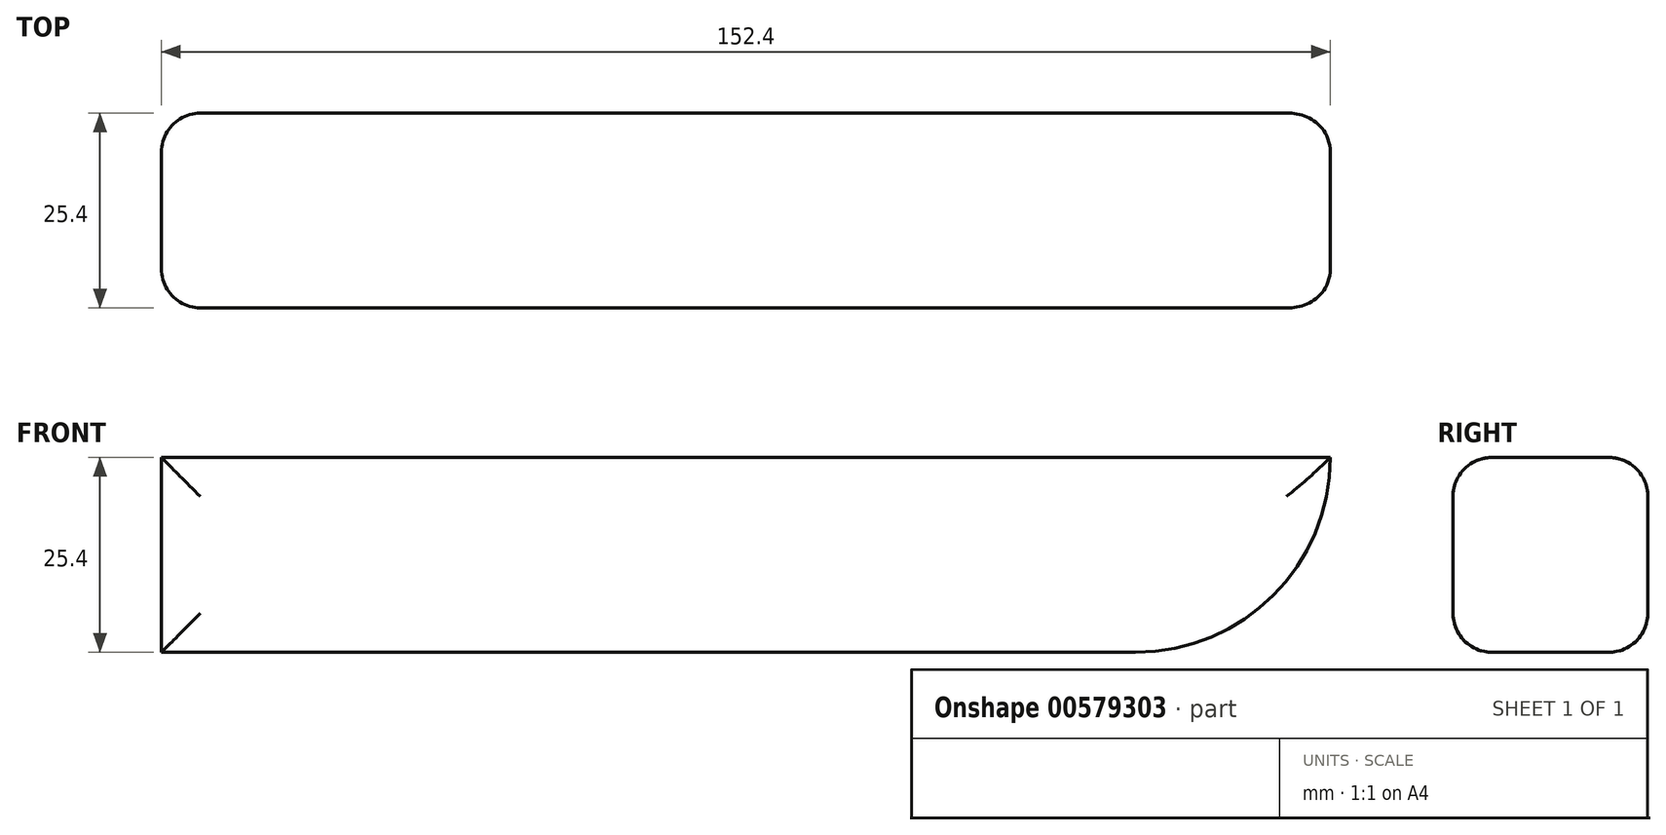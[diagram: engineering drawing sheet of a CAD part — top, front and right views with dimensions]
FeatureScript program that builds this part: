
annotation { "Feature Type Name" : "Feature", "Feature Type Description" : "" }
export const myFeature = defineFeature(function(context is Context, id is Id, definition is map)
    precondition{}
    {
        {
            var Q0;
            Q0=qCreatedBy(makeId("Front.planeOp"),FACE);
            var sketch = newSketch(context, id + "F0", { "sketchPlane" : qUnion([Q0])});
            skLineSegment(sketch, "E0.bottom", {"start": v(-75.73, -10.02) * mm, "end": v(51.27, -10.02) * mm});
            skLineSegment(sketch, "E0.top", {"start": v(-75.73, -35.42) * mm, "end": v(51.27, -35.42) * mm});
            skLineSegment(sketch, "E0.left", {"start": v(-75.73, -10.02) * mm, "end": v(-75.73, -35.42) * mm});
            skLineSegment(sketch, "E0.right", {"start": v(51.27, -10.02) * mm, "end": v(51.27, -35.42) * mm});
            skLineSegment(sketch, "E1", {"start": v(51.27, -10.02) * mm, "end": v(76.67, -10.02) * mm});
            skArc(sketch, "E2", {"start": v(51.27, -35.42) * mm, "mid": v(69.23, -27.98) * mm, "end": v(76.67, -10.02) * mm});
            skSolve(sketch);
        }
        {
            var Q0;
            Q0 = qSketchRegion(id + "F0", true);
            var Q1;
            Q1 = qSketchRegion(id + "FrB0VU85BViKOfO_0", true);
            extrude(context, id + "F1", {"entities" : qUnion([Q0, Q1]), "depth" : 25.4 * mm, "offsetDistance" : 25.4 * mm});
        }
        {
            var Q0;
            Q0=makeQuery(id+"F1.opExtrude","CAP_FACE",FACE,{"disambiguationData":[OSD([sQuery(id+"F0.wireOp",EDGE,"E0.bottom"),sQuery(id+"F0.wireOp",EDGE,"E0.top"),sQuery(id+"F0.wireOp",EDGE,"E0.left"),sQuery(id+"F0.wireOp",EDGE,"E1"),sQuery(id+"F0.wireOp",EDGE,"E2")])],"isStart":false});
            var Q1;
            Q1=makeQuery(id+"F1.opExtrude","CAP_FACE",FACE,{"disambiguationData":[OSD([sQuery(id+"F0.wireOp",EDGE,"E0.bottom"),sQuery(id+"F0.wireOp",EDGE,"E0.top"),sQuery(id+"F0.wireOp",EDGE,"E0.left"),sQuery(id+"F0.wireOp",EDGE,"E1"),sQuery(id+"F0.wireOp",EDGE,"E2")])],"isStart":true});
            fillet(context, id + "F2", {"entities" : qUnion([Q0, Q1]), "radius" : 5.08 * mm, "tangentPropagation" : true, "allowEdgeOverflow" : false});
        }
    });
